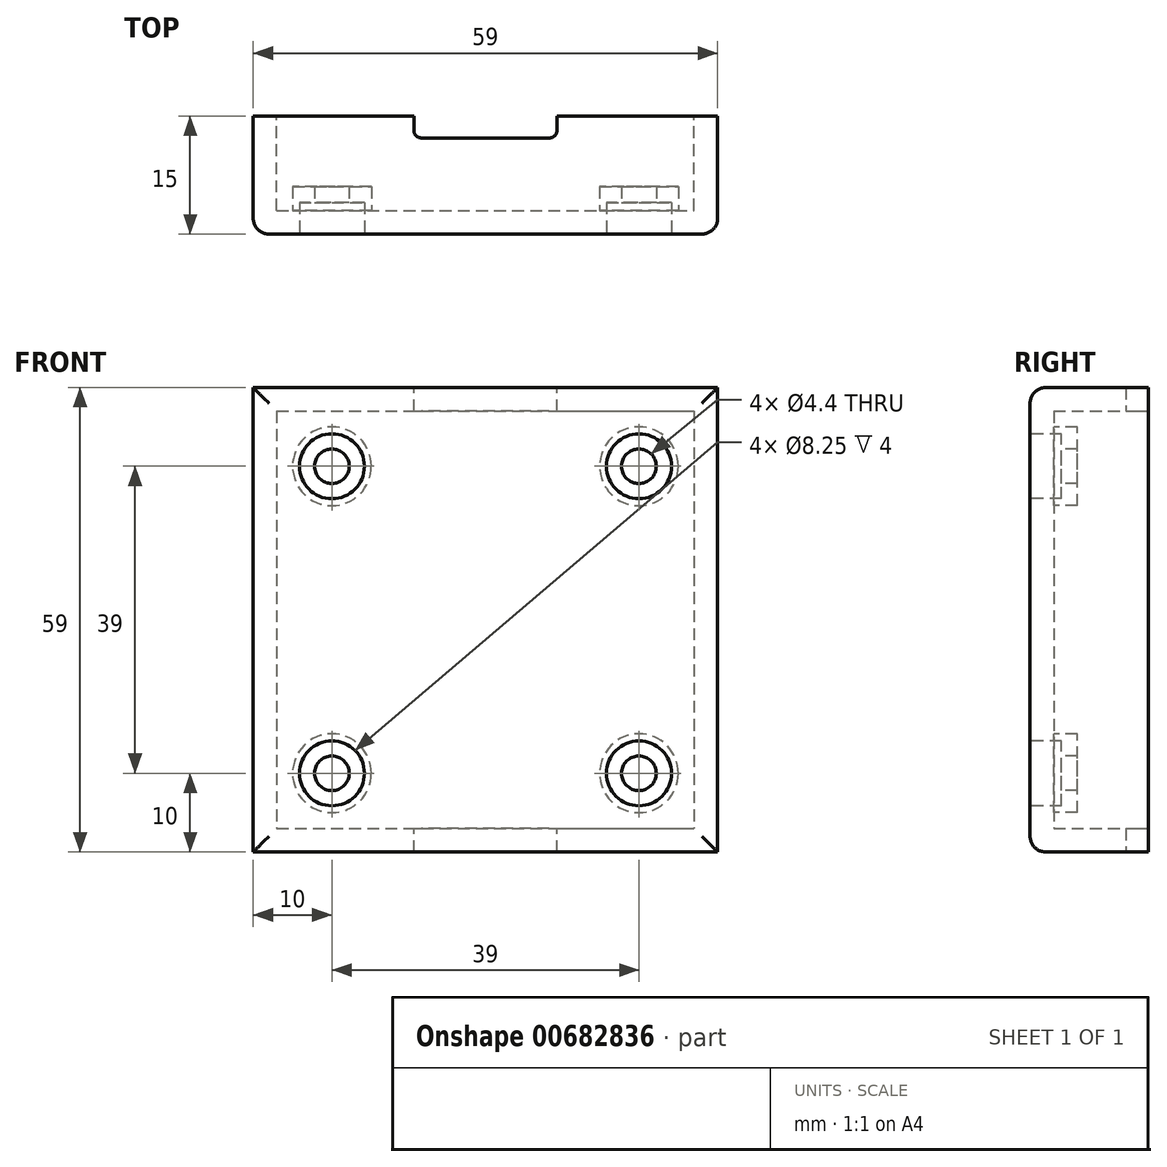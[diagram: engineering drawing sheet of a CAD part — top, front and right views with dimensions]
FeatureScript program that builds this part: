
annotation { "Feature Type Name" : "Feature", "Feature Type Description" : "" }
export const myFeature = defineFeature(function(context is Context, id is Id, definition is map)
    precondition{}
    {
        {
            var Q0;
            Q0=qCreatedBy(makeId("Front.planeOp"),FACE);
            var sketch = newSketch(context, id + "F0", { "sketchPlane" : qUnion([Q0])});
            skLineSegment(sketch, "E0.bottom", {"start": v(-29.5, 29.5) * mm, "end": v(29.5, 29.5) * mm});
            skLineSegment(sketch, "E0.top", {"start": v(-29.5, -29.5) * mm, "end": v(29.5, -29.5) * mm});
            skLineSegment(sketch, "E0.left", {"start": v(-29.5, 29.5) * mm, "end": v(-29.5, -29.5) * mm});
            skLineSegment(sketch, "E0.right", {"start": v(29.5, 29.5) * mm, "end": v(29.5, -29.5) * mm});
            skSolve(sketch);
        }
        {
            var Q0;
            Q0=qCreatedBy(makeId("Front.planeOp"),FACE);
            var sketch = newSketch(context, id + "F1", { "sketchPlane" : qUnion([Q0])});
            skLineSegment(sketch, "E1.bottom", {"start": v(-26.5, 26.5) * mm, "end": v(26.5, 26.5) * mm});
            skLineSegment(sketch, "E1.top", {"start": v(-26.5, -26.5) * mm, "end": v(26.5, -26.5) * mm});
            skLineSegment(sketch, "E1.left", {"start": v(-26.5, 26.5) * mm, "end": v(-26.5, -26.5) * mm});
            skLineSegment(sketch, "E1.right", {"start": v(26.5, 26.5) * mm, "end": v(26.5, -26.5) * mm});
            skSolve(sketch);
        }
        {
            var Q0;
            Q0=qCreatedBy(makeId("Top.planeOp"),FACE);
            var sketch = newSketch(context, id + "F2", { "sketchPlane" : qUnion([Q0])});
            skLineSegment(sketch, "E2.bottom", {"start": v(-8.1, 2.8) * mm, "end": v(8.1, 2.8) * mm});
            skLineSegment(sketch, "E2.top", {"start": v(-8.1, -2.8) * mm, "end": v(8.1, -2.8) * mm});
            skLineSegment(sketch, "E2.left", {"start": v(-9.1, 1.8) * mm, "end": v(-9.1, -1.8) * mm});
            skLineSegment(sketch, "E2.right", {"start": v(9.1, 1.8) * mm, "end": v(9.1, -1.8) * mm});
            skPoint(sketch, "E3.visualSharp", {"position": v(-9.1, -2.8) * mm});
            skArc(sketch, "E3.filletArc", {"start": v(-9.1, -1.8) * mm, "mid": v(-8.8, -2.5) * mm, "end": v(-8.1, -2.8) * mm});
            skPoint(sketch, "E4.visualSharp", {"position": v(9.1, -2.8) * mm});
            skArc(sketch, "E4.filletArc", {"start": v(8.1, -2.8) * mm, "mid": v(8.8, -2.5) * mm, "end": v(9.1, -1.8) * mm});
            skPoint(sketch, "E5.visualSharp", {"position": v(9.1, 2.8) * mm});
            skArc(sketch, "E5.filletArc", {"start": v(9.1, 1.8) * mm, "mid": v(8.8, 2.5) * mm, "end": v(8.1, 2.8) * mm});
            skPoint(sketch, "E6.visualSharp", {"position": v(-9.1, 2.8) * mm});
            skArc(sketch, "E6.filletArc", {"start": v(-8.1, 2.8) * mm, "mid": v(-8.8, 2.5) * mm, "end": v(-9.1, 1.8) * mm});
            skSolve(sketch);
        }
        {
            var Q0;
            Q0=qSketchRegion(id+"F0",true);
            extrude(context, id + "F3", {"entities" : qUnion([Q0]), "depth" : 15 * mm, "offsetDistance" : 25 * mm});
        }
        {
            var Q0;
            Q0=qSketchRegion(id+"F1",true);
            extrude(context, id + "F4", {"entities" : qUnion([Q0]), "operationType" : NewBodyOperationType.REMOVE, "depth" : 12 * mm, "offsetDistance" : 25 * mm});
        }
        {
            var Q0;
            Q0=makeQuery(id+"F3.opExtrude","CAP_FACE",FACE,{"disambiguationData":[OSD([sQuery(id+"F0.wireOp",EDGE,"E0.bottom"),sQuery(id+"F0.wireOp",EDGE,"E0.top"),sQuery(id+"F0.wireOp",EDGE,"E0.left"),sQuery(id+"F0.wireOp",EDGE,"E0.right")])],"isStart":false});
            fillet(context, id + "F5", {"entities" : qUnion([Q0]), "radius" : 2 * mm, "tangentPropagation" : true, "allowEdgeOverflow" : false});
        }
        {
            var Q0;
            Q0=qCreatedBy(makeId("Front.planeOp"),FACE);
            cPlane(context, id + "F6", {"entities" : qUnion([Q0]), "cplaneType" : CPlaneType.OFFSET, "offset" : 15 * mm, "width" : 150 * mm, "height" : 150 * mm});
        }
        {
            var Q0;
            Q0=qCreatedBy(id+"F6.planeOp",FACE);
            var sketch = newSketch(context, id + "F7", { "sketchPlane" : qUnion([Q0])});
            skCircle(sketch, "E7", {"center": v(19.5, 19.5) * mm, "radius": 5 * mm});
            skCircle(sketch, "E8.MirrorC", {"center": v(-19.5, 19.5) * mm, "radius": 5 * mm});
            skCircle(sketch, "E9.MirrorC", {"center": v(19.5, -19.5) * mm, "radius": 5 * mm});
            skCircle(sketch, "E10.MirrorC", {"center": v(-19.5, -19.5) * mm, "radius": 5 * mm});
            skSolve(sketch);
        }
        {
            var Q0;
            Q0=qSketchRegion(id+"F7",true);
            extrude(context, id + "F8", {"entities" : qUnion([Q0]), "operationType" : NewBodyOperationType.ADD, "oppositeDirection" : true, "depth" : 6 * mm, "offsetDistance" : 25 * mm});
        }
        {
            var Q0;
            Q0=qCreatedBy(id+"F6.planeOp",FACE);
            var sketch = newSketch(context, id + "F9", { "sketchPlane" : qUnion([Q0])});
            skPoint(sketch, "E11", {"position": v(-19.5, 19.5) * mm});
            skPoint(sketch, "E12", {"position": v(19.5, 19.5) * mm});
            skPoint(sketch, "E13", {"position": v(19.5, -19.5) * mm});
            skPoint(sketch, "E14", {"position": v(-19.5, -19.5) * mm});
            skSolve(sketch);
        }
        {
            var Q0;
            Q0=sQuery(id+"F9.wireOp",VERTEX,"E11");
            var Q1;
            Q1=makeQuery(id+"F3.opExtrude","SWEPT_BODY",BODY,{"disambiguationData":[OSD([sQuery(id+"F0.wireOp",EDGE,"E0.bottom"),sQuery(id+"F0.wireOp",EDGE,"E0.top"),sQuery(id+"F0.wireOp",EDGE,"E0.left"),sQuery(id+"F0.wireOp",EDGE,"E0.right")])]});
            hole(context, id + "F10", {"style" : HoleStyle.C_BORE, "endStyle" : HoleEndStyle.THROUGH, "standardTappedOrClearance" : lookupTablePath({ "standard" : "ISO", "fit" : "Normal", "size" : "M4", "type" : "Clearance" }), "standardBlindInLast" : lookupTablePath({ "fit" : "Standard", "standard" : "ISO", "size" : "M4", "type" : "Clearance" }), "holeDiameter" : 4.4 * mm, "cBoreDiameter" : 8.25 * mm, "cBoreDepth" : 4 * mm, "majorDiameter" : 5 * mm, "isTappedThrough" : true, "tappedDepth" : 12 * mm, "tapClearance" : 3, "locations" : qUnion([Q0]), "scope" : qUnion([Q1])});
        }
        {
            var Q0;
            Q0=sQuery(id+"F9.wireOp",VERTEX,"E14");
            var Q1;
            Q1=makeQuery(id+"F3.opExtrude","SWEPT_BODY",BODY,{"disambiguationData":[OSD([sQuery(id+"F0.wireOp",EDGE,"E0.bottom"),sQuery(id+"F0.wireOp",EDGE,"E0.top"),sQuery(id+"F0.wireOp",EDGE,"E0.left"),sQuery(id+"F0.wireOp",EDGE,"E0.right")])]});
            hole(context, id + "F11", {"style" : HoleStyle.C_BORE, "endStyle" : HoleEndStyle.THROUGH, "standardTappedOrClearance" : lookupTablePath({ "standard" : "ISO", "fit" : "Normal", "size" : "M4", "type" : "Clearance" }), "standardBlindInLast" : lookupTablePath({ "fit" : "Standard", "standard" : "ISO", "size" : "M4", "type" : "Clearance" }), "holeDiameter" : 4.4 * mm, "cBoreDiameter" : 8.25 * mm, "cBoreDepth" : 4 * mm, "majorDiameter" : 5 * mm, "isTappedThrough" : true, "tappedDepth" : 12 * mm, "tapClearance" : 3, "locations" : qUnion([Q0]), "scope" : qUnion([Q1])});
        }
        {
            var Q0;
            Q0=sQuery(id+"F9.wireOp",VERTEX,"E13");
            var Q1;
            Q1=makeQuery(id+"F3.opExtrude","SWEPT_BODY",BODY,{"disambiguationData":[OSD([sQuery(id+"F0.wireOp",EDGE,"E0.bottom"),sQuery(id+"F0.wireOp",EDGE,"E0.top"),sQuery(id+"F0.wireOp",EDGE,"E0.left"),sQuery(id+"F0.wireOp",EDGE,"E0.right")])]});
            hole(context, id + "F12", {"style" : HoleStyle.C_BORE, "endStyle" : HoleEndStyle.THROUGH, "standardTappedOrClearance" : lookupTablePath({ "standard" : "ISO", "fit" : "Normal", "size" : "M4", "type" : "Clearance" }), "standardBlindInLast" : lookupTablePath({ "fit" : "Standard", "standard" : "ISO", "size" : "M4", "type" : "Clearance" }), "holeDiameter" : 4.4 * mm, "cBoreDiameter" : 8.25 * mm, "cBoreDepth" : 4 * mm, "majorDiameter" : 5 * mm, "isTappedThrough" : true, "tappedDepth" : 12 * mm, "tapClearance" : 3, "locations" : qUnion([Q0]), "scope" : qUnion([Q1])});
        }
        {
            var Q0;
            Q0=sQuery(id+"F9.wireOp",VERTEX,"E12");
            var Q1;
            Q1=makeQuery(id+"F3.opExtrude","SWEPT_BODY",BODY,{"disambiguationData":[OSD([sQuery(id+"F0.wireOp",EDGE,"E0.bottom"),sQuery(id+"F0.wireOp",EDGE,"E0.top"),sQuery(id+"F0.wireOp",EDGE,"E0.left"),sQuery(id+"F0.wireOp",EDGE,"E0.right")])]});
            hole(context, id + "F13", {"style" : HoleStyle.C_BORE, "endStyle" : HoleEndStyle.THROUGH, "standardTappedOrClearance" : lookupTablePath({ "standard" : "ISO", "fit" : "Normal", "size" : "M4", "type" : "Clearance" }), "standardBlindInLast" : lookupTablePath({ "fit" : "Standard", "standard" : "ISO", "size" : "M4", "type" : "Clearance" }), "holeDiameter" : 4.4 * mm, "cBoreDiameter" : 8.25 * mm, "cBoreDepth" : 4 * mm, "majorDiameter" : 5 * mm, "isTappedThrough" : true, "tappedDepth" : 12 * mm, "tapClearance" : 3, "locations" : qUnion([Q0]), "scope" : qUnion([Q1])});
        }
        {
            var Q0;
            Q0 = qSketchRegion(id + "F2", true);
            extrude(context, id + "F14", {"entities" : qUnion([Q0]), "operationType" : NewBodyOperationType.REMOVE, "endBound" : BoundingType.SYMMETRIC, "depth" : 60 * mm, "offsetDistance" : 25 * mm});
        }
    });
